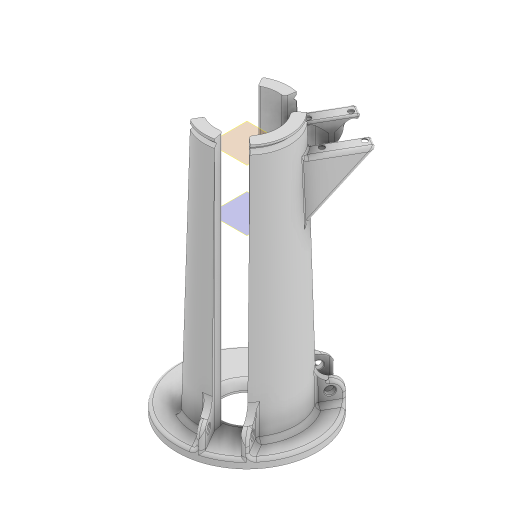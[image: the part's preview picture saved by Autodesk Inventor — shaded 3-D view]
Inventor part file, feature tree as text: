
AUTODESK INVENTOR PART (.ipt)
format: ipt  version: 2023 (Build 270158000, 158)  size: 1,888,256 bytes
history: native  units: in
note: dims shown in document units (in); Inventor stores cm internally (conversion verified against a paired STEP export)
features: fillet x14, projected_geometry x8, sketch x6, plane x6, extrude x4, hole x2, draft x2, pattern_circular x1, revolve x1, chamfer x1, mirror x1
ambient origin geometry x8: Origin, YZ Plane, XZ Plane, XY Plane, X Axis, Y Axis, Z Axis, Center Point
bodies: Solid1 (feature_tree)
feature tree (46):
  sketch  "Sketch2"  dims[d0=1.0in d1=1.4038in]
  extrude  "Extrusion1"  Depth=1.4038in
  extrude  "Extrusion2"  TaperAngle=120.0deg  [1 undecoded]
  extrude  "Extrusion3"  Depth=0.481in
  hole  "Hole1"  [1 undecoded]
  pattern_circular  "Circular Pattern1"  [2 undecoded]
  sketch  "Sketch5"  dims[d4=0.5906in d5=0.481in]
  fillet  "Fillet1"  Radius=5.9055in
  plane  "Work Plane3"
  plane  "Work Plane2"
  revolve  "Revolution1"  [1 undecoded]
  draft  "FaceDraft6"
  plane  "Work Plane6"
  plane  "Work Plane7"
  plane  "Work Plane5"
  sketch  "Sketch16"  dims[d13=120.0deg d14=0.1969in d15=0.0in d17=5.9055in d18=0.0in d19=0.1378in d20=0.1378in d21=0.5906in d22=0.4961in d23=0.0in d24=0.7874in d25=120.0deg d28=0.1831in d29=0.2362in d30=0.1575in d31=0.0787in d32=90.0deg d33=0.315in d34=0.8108in d35=0.3937in d39=1.0945in d40=0.0787in d66=0.1181in d67=0.0787in d68=360.0deg d69=-0.6427in d70=1.1024in d72=0.3228in d73=0.7087in d74=0.1736in d76=0.122in d77=0.122in d82=0.2953in d83=0.2559in d84=0.2362in d85=0.1575in d86=0.0787in d87=90.0deg d88=1.2992in d89=90.0deg d104=0.1831in d107=0.0103in d123=0.2756in d124=0.0984in d125=0.1575in d126=0.0787in d127=0.0157in d128=0.0787in d129=45.0deg d146=0.6118in d147=90.0deg d148=90.0deg d150=1.378in d151=0.0in d152=-0.2886in d153=0.1171in d154=0.1171in d155=0.0394in d156=0.3937in d157=0.1969in d158=0.3937in d159=0.0394in d160=0.0787in d161=0.0689in d162=0.0787in d163=0.0394in d106=0.0197in d108=0.0197in d109=0.0344in d113=0.0197in d114=0.0344in d115=0.0197in d116=0.0344in]
  fillet  "Fillet15"  Radius=0.1378in
  fillet  "Fillet16"  Radius=0.5906in
  fillet  "Fillet17"  Radius=0.4961in
  fillet  "Fillet18"  Radius=0.7874in
  chamfer  "Chamfer1"  Distance=0.3937in
  sketch  "Sketch11"  dims[d11=0.8987in]
  extrude  "Extrusion14"  Depth=1.0945in
  hole  "Hole3"  [1 undecoded]
  plane  "Work Plane4"
  draft  "FaceDraft8"
  mirror  "Mirror4"
  fillet  "Fillet21"  Radius=0.1181in
  fillet  "Fillet22"  Radius=0.0787in
  fillet  "Fillet23"  [1 undecoded]
  fillet  "Fillet24"  [1 undecoded]
  fillet  "Fillet25"  Radius=1.1024in
  fillet  "Fillet26"  Radius=0.3228in
  fillet  "Fillet27"  Radius=0.7087in
  fillet  "Fillet28"  Radius=0.1736in
  fillet  "Fillet29"  Radius=0.122in
  sketch  "Sketch3"  dims[d2=3.1496in d3=120.0deg]
  projected_geometry  "Projected Loop1"
  projected_geometry  "Projected Loop2"
  projected_geometry  "Projected Loop3"
  projected_geometry  "Projected Loop4"
  projected_geometry  "Projected Loop5"
  sketch  "Sketch10"  dims[d6=0.8987in d7=0.7874in d9=120.0deg]
  projected_geometry  "Projected Loop8"
  projected_geometry  "Project Cut Edges1"
  projected_geometry  "Project Cut Edges2"
note: 8 required parameter values undecoded (feature->parameter linkage not recoverable at this tier; creation-order binding heuristic only, values carry confidence <= 0.55)